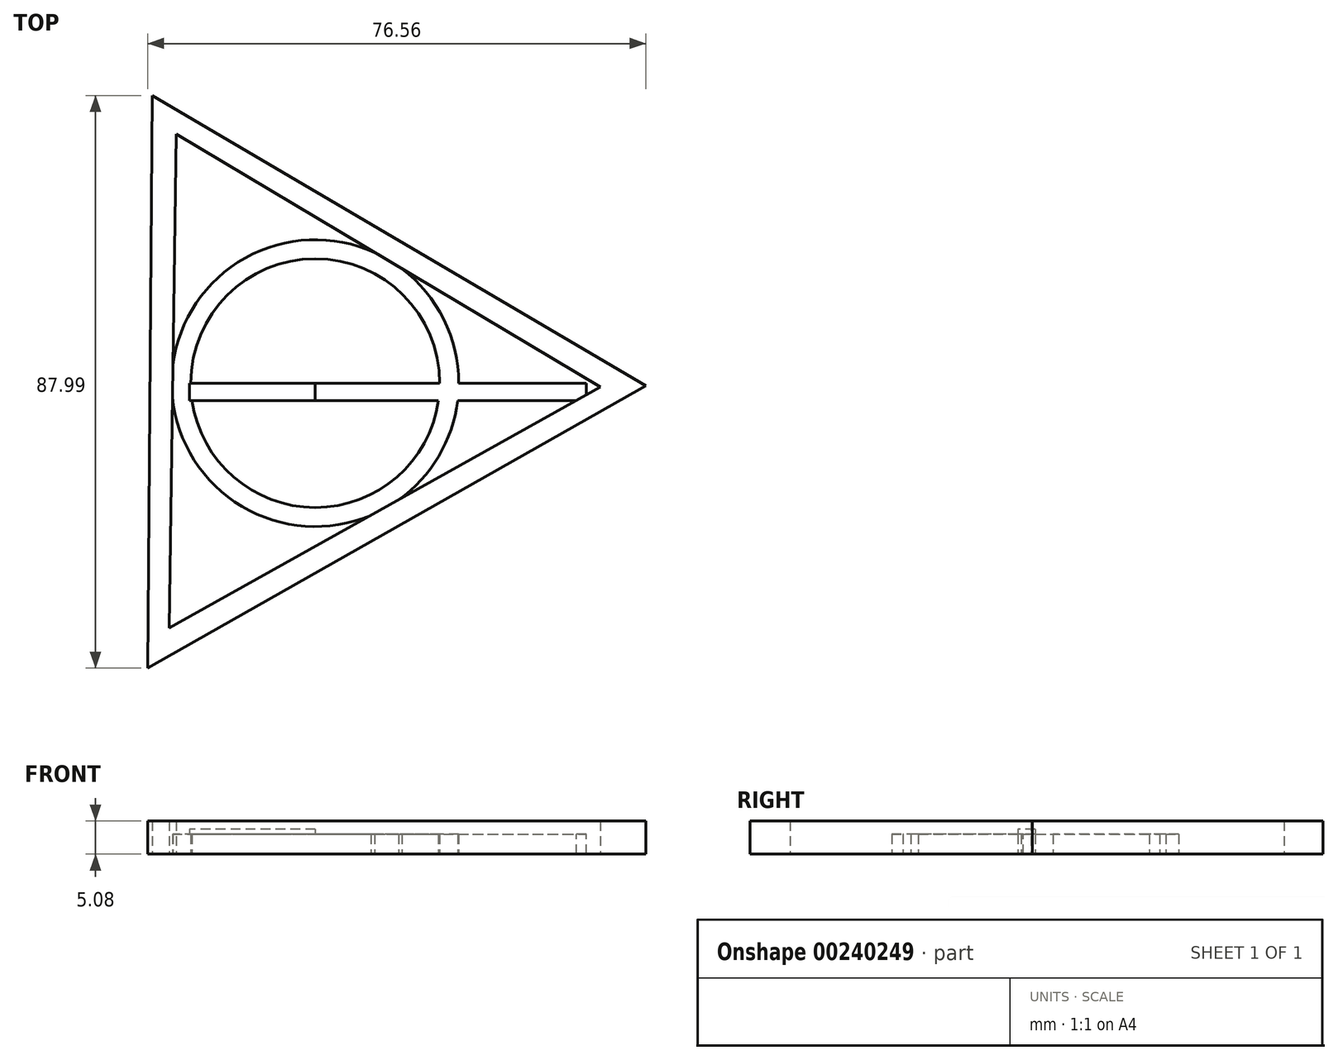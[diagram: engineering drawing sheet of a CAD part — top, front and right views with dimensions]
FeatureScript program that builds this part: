
annotation { "Feature Type Name" : "Feature", "Feature Type Description" : "" }
export const myFeature = defineFeature(function(context is Context, id is Id, definition is map)
    precondition{}
    {
        {
            var Q0;
            Q0=qCreatedBy(makeId("Top.planeOp"),FACE);
            var sketch = newSketch(context, id + "F0", { "sketchPlane" : qUnion([Q0])});
            skCircle(sketch, "E0.cCircle", {"center": v(0, 0) * mm, "radius": 25.4 * mm, "construction": true});
            skLineSegment(sketch, "E0.0", {"start": v(-25.04, 44.2) * mm, "end": v(50.8, -0.41) * mm});
            skLineSegment(sketch, "E0.1", {"start": v(50.8, -0.41) * mm, "end": v(-25.76, -43.79) * mm});
            skLineSegment(sketch, "E0.2", {"start": v(-25.76, -43.79) * mm, "end": v(-25.04, 44.2) * mm});
            skPoint(sketch, "E0.0.midPoint", {"position": v(12.88, 21.9) * mm});
            skCircle(sketch, "E1.cCircle", {"center": v(0, 0) * mm, "radius": 21.9 * mm, "construction": true});
            skLineSegment(sketch, "E1.0", {"start": v(-22.44, -37.63) * mm, "end": v(-21.37, 38.24) * mm});
            skLineSegment(sketch, "E1.1", {"start": v(-21.37, 38.24) * mm, "end": v(43.8, -0.62) * mm});
            skLineSegment(sketch, "E1.2", {"start": v(43.8, -0.62) * mm, "end": v(-22.44, -37.63) * mm});
            skPoint(sketch, "E1.0.midPoint", {"position": v(-21.9, 0.3) * mm});
            skSolve(sketch);
        }
        {
            var Q0;
            Q0=makeQuery(id+"F0.imprint","IMPRINT",FACE,{"disambiguationData":[TD([[makeQuery(id+"F0.imprint","IMPRINT",EDGE,{"derivedFrom":sQuery(id+"F0.wireOp",EDGE,"E0.0")}),-1.0]])]});
            extrude(context, id + "F1", {"entities" : qUnion([Q0]), "depth" : 5.08 * mm});
        }
        {
            var Q0;
            Q0=qCreatedBy(makeId("Top.planeOp"),FACE);
            var sketch = newSketch(context, id + "F2", { "sketchPlane" : qUnion([Q0])});
            skCircle(sketch, "E2", {"center": v(0, 0) * mm, "radius": 22.04 * mm});
            skCircle(sketch, "E3", {"center": v(0, 0) * mm, "radius": 19.11 * mm});
            skSolve(sketch);
        }
        {
            var Q0;
            Q0=makeQuery(id+"F2.imprint","IMPRINT",FACE,{"disambiguationData":[TD([[makeQuery(id+"F2.imprint","IMPRINT",EDGE,{"derivedFrom":sQuery(id+"F2.wireOp",EDGE,"E2")}),1.0]])]});
            extrude(context, id + "F3", {"entities" : qUnion([Q0]), "operationType" : NewBodyOperationType.ADD, "depth" : 3.05 * mm});
        }
        {
            var Q0;
            Q0=qCreatedBy(makeId("Top.planeOp"),FACE);
            var sketch = newSketch(context, id + "F4", { "sketchPlane" : qUnion([Q0])});
            skLineSegment(sketch, "E4.bottom", {"start": v(0, 0) * mm, "end": v(41.64, 0) * mm});
            skLineSegment(sketch, "E4.top", {"start": v(0, -2.67) * mm, "end": v(41.64, -2.67) * mm});
            skLineSegment(sketch, "E4.left", {"start": v(0, 0) * mm, "end": v(0, -2.67) * mm});
            skLineSegment(sketch, "E4.right", {"start": v(41.64, 0) * mm, "end": v(41.64, -2.67) * mm});
            skLineSegment(sketch, "E5.bottom", {"start": v(0, 0) * mm, "end": v(-19.3, 0) * mm});
            skLineSegment(sketch, "E5.top", {"start": v(0, -2.67) * mm, "end": v(-19.3, -2.67) * mm});
            skLineSegment(sketch, "E5.right", {"start": v(-19.3, 0) * mm, "end": v(-19.3, -2.67) * mm});
            skSolve(sketch);
        }
        {
            var Q0;
            Q0=makeQuery(id+"F4.imprint","IMPRINT",FACE,{"disambiguationData":[TD([[makeQuery(id+"F4.imprint","IMPRINT",EDGE,{"derivedFrom":sQuery(id+"F4.wireOp",EDGE,"E5.bottom")}),1.0]])]});
            extrude(context, id + "F5", {"entities" : qUnion([Q0]), "operationType" : NewBodyOperationType.ADD, "depth" : 3.8 * mm});
        }
        {
            var Q0;
            Q0 = qSketchRegion(id + "F4", true);
            extrude(context, id + "F6", {"entities" : qUnion([Q0]), "operationType" : NewBodyOperationType.ADD, "depth" : 3.05 * mm});
        }
    });
